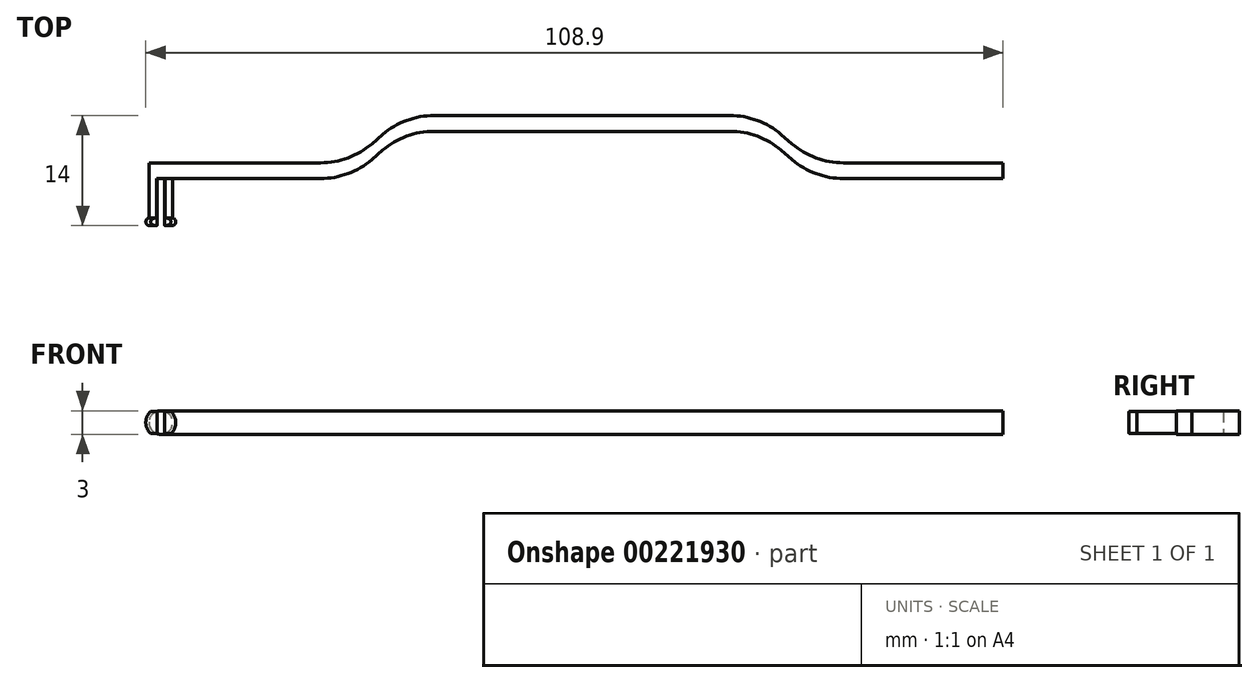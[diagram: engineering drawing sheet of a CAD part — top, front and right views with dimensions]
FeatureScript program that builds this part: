
annotation { "Feature Type Name" : "Feature", "Feature Type Description" : "" }
export const myFeature = defineFeature(function(context is Context, id is Id, definition is map)
    precondition{}
    {
        {
            var Q0;
            Q0=qCreatedBy(makeId("Top.planeOp"),FACE);
            var sketch = newSketch(context, id + "F0", { "sketchPlane" : qUnion([Q0])});
            skLineSegment(sketch, "E0.bottom", {"start": v(-53.5, 0) * mm, "end": v(-29.5, 0) * mm});
            skLineSegment(sketch, "E0.top", {"start": v(-53.5, 2) * mm, "end": v(-29.5, 2) * mm});
            skLineSegment(sketch, "E0.left", {"start": v(-53.5, 0) * mm, "end": v(-53.5, 2) * mm});
            skLineSegment(sketch, "E0.right", {"start": v(-29.5, 0) * mm, "end": v(-29.5, 2) * mm});
            skLineSegment(sketch, "E1.MirrorCS", {"start": v(29.5, 0) * mm, "end": v(29.5, 2) * mm});
            skLineSegment(sketch, "E2.MirrorCS", {"start": v(53.5, 0) * mm, "end": v(53.5, 2) * mm});
            skLineSegment(sketch, "E3.MirrorCS", {"start": v(53.5, 2) * mm, "end": v(29.5, 2) * mm});
            skLineSegment(sketch, "E4.MirrorCS", {"start": v(53.5, 0) * mm, "end": v(29.5, 0) * mm});
            skLineSegment(sketch, "E5.bottom", {"start": v(-22.5, 8) * mm, "end": v(0, 8) * mm});
            skLineSegment(sketch, "E5.top", {"start": v(-22.5, 6) * mm, "end": v(0, 6) * mm});
            skLineSegment(sketch, "E5.left", {"start": v(-22.5, 8) * mm, "end": v(-22.5, 6) * mm});
            skLineSegment(sketch, "E5.right", {"start": v(0, 8) * mm, "end": v(0, 6) * mm});
            skLineSegment(sketch, "E6.MirrorCS", {"start": v(22.5, 8) * mm, "end": v(22.5, 6) * mm});
            skLineSegment(sketch, "E7.MirrorCS", {"start": v(22.5, 8) * mm, "end": v(0, 8) * mm});
            skLineSegment(sketch, "E8.MirrorCS", {"start": v(22.5, 6) * mm, "end": v(0, 6) * mm});
            skLineSegment(sketch, "E9", {"start": v(-29.5, 0) * mm, "end": v(-22.5, 6) * mm});
            skLineSegment(sketch, "E10", {"start": v(-29.5, 2) * mm, "end": v(-22.5, 8) * mm});
            skLineSegment(sketch, "E11.MirrorCS", {"start": v(29.5, 0) * mm, "end": v(22.5, 6) * mm});
            skLineSegment(sketch, "E12.MirrorCS", {"start": v(29.5, 2) * mm, "end": v(22.5, 8) * mm});
            skLineSegment(sketch, "E13", {"start": v(-22.5, 8) * mm, "end": v(-29.5, 8) * mm, "construction": true});
            skLineSegment(sketch, "E14", {"start": v(22.5, 8) * mm, "end": v(29.5, 8) * mm, "construction": true});
            skSolve(sketch);
        }
        {
            var Q0;
            Q0 = qSketchRegion(id + "F0", true);
            extrude(context, id + "F1", {"entities" : qUnion([Q0]), "depth" : 3 * mm});
        }
        {
            var Q0;
            Q0=makeQuery(id+"F1.opExtrude","SWEPT_EDGE",EDGE,{"disambiguationData":[OSD([sQuery(id+"F0.wireOp",EDGE,"E0.top"),sQuery(id+"F0.wireOp",EDGE,"E0.right"),sQuery(id+"F0.wireOp",EDGE,"E10")])]});
            var Q1;
            Q1=makeQuery(id+"F1.opExtrude","SWEPT_EDGE",EDGE,{"disambiguationData":[OSD([sQuery(id+"F0.wireOp",EDGE,"E5.bottom"),sQuery(id+"F0.wireOp",EDGE,"E5.left"),sQuery(id+"F0.wireOp",EDGE,"E10")])]});
            var Q2;
            Q2=makeQuery(id+"F1.opExtrude","SWEPT_EDGE",EDGE,{"disambiguationData":[OSD([sQuery(id+"F0.wireOp",EDGE,"E7.MirrorCS"),sQuery(id+"F0.wireOp",EDGE,"E6.MirrorCS"),sQuery(id+"F0.wireOp",EDGE,"E12.MirrorCS")])]});
            var Q3;
            Q3=makeQuery(id+"F1.opExtrude","SWEPT_EDGE",EDGE,{"disambiguationData":[OSD([sQuery(id+"F0.wireOp",EDGE,"E3.MirrorCS"),sQuery(id+"F0.wireOp",EDGE,"E1.MirrorCS"),sQuery(id+"F0.wireOp",EDGE,"E12.MirrorCS")])]});
            var Q4;
            Q4=makeQuery(id+"F1.opExtrude","SWEPT_EDGE",EDGE,{"disambiguationData":[OSD([sQuery(id+"F0.wireOp",EDGE,"E4.MirrorCS"),sQuery(id+"F0.wireOp",EDGE,"E11.MirrorCS"),sQuery(id+"F0.wireOp",EDGE,"E1.MirrorCS")])]});
            var Q5;
            Q5=makeQuery(id+"F1.opExtrude","SWEPT_EDGE",EDGE,{"disambiguationData":[OSD([sQuery(id+"F0.wireOp",EDGE,"E8.MirrorCS"),sQuery(id+"F0.wireOp",EDGE,"E6.MirrorCS"),sQuery(id+"F0.wireOp",EDGE,"E11.MirrorCS")])]});
            var Q6;
            Q6=makeQuery(id+"F1.opExtrude","SWEPT_EDGE",EDGE,{"disambiguationData":[OSD([sQuery(id+"F0.wireOp",EDGE,"E5.top"),sQuery(id+"F0.wireOp",EDGE,"E5.left"),sQuery(id+"F0.wireOp",EDGE,"E9")])]});
            var Q7;
            Q7=makeQuery(id+"F1.opExtrude","SWEPT_EDGE",EDGE,{"disambiguationData":[OSD([sQuery(id+"F0.wireOp",EDGE,"E0.bottom"),sQuery(id+"F0.wireOp",EDGE,"E0.right"),sQuery(id+"F0.wireOp",EDGE,"E9")])]});
            fillet(context, id + "F2", {"entities" : qUnion([Q0, Q1, Q2, Q3, Q4, Q5, Q6, Q7]), "radius" : 10 * mm, "tangentPropagation" : true, "allowEdgeOverflow" : false});
        }
        {
            var Q0;
            Q0=makeQuery(id+"F1.opExtrude","SWEPT_FACE",FACE,{"disambiguationData":[OSD([sQuery(id+"F0.wireOp",EDGE,"E0.bottom")])]});
            var sketch = newSketch(context, id + "F3", { "sketchPlane" : qUnion([Q0])});
            skCircle(sketch, "E15", {"center": v(-53.5, 1.5) * mm, "radius": 1.5 * mm});
            skCircle(sketch, "E16.MirrorC", {"center": v(53.5, 1.5) * mm, "radius": 1.5 * mm});
            skSolve(sketch);
        }
        {
            var Q0;
            {var subQ1=sQuery(id+"F0.wireOp",EDGE,"E0.bottom");var subQ2=makeQuery(id+"F1.opExtrude","SWEPT_EDGE",EDGE,{"disambiguationData":[OSD([subQ1,sQuery(id+"F0.wireOp",EDGE,"E0.left")])]});Q0=makeQuery(id+"F3.imprint","IMPRINT",FACE,{"disambiguationData":[TD([[makeQuery(id+"F3.imprint","IMPRINT",EDGE,{"derivedFrom":subQ2}),-1.0]])]});}
            var Q1;
            Q1=makeQuery(id+"F3.imprint","IMPRINT",FACE,{"disambiguationData":[TD([[makeQuery(id+"F3.imprint","IMPRINT",EDGE,{"derivedFrom":sQuery(id+"F3.wireOp",EDGE,"E16.MirrorC")}),-1.0]])]});
            var Q2;
            Q2=makeQuery(id+"F1.opExtrude","SWEPT_FACE",FACE,{"disambiguationData":[OSD([sQuery(id+"F0.wireOp",EDGE,"E0.top")])]});
            extrude(context, id + "F4", {"entities" : qUnion([Q0, Q1]), "operationType" : NewBodyOperationType.ADD, "endBound" : BoundingType.UP_TO_SURFACE, "oppositeDirection" : true, "endBoundEntityFace" : qUnion([Q2]), "depth" : 25 * mm});
        }
        {
            var Q0;
            {var subQ1=sQuery(id+"F0.wireOp",EDGE,"E0.bottom");var subQ2=makeQuery(id+"F1.opExtrude","SWEPT_EDGE",EDGE,{"disambiguationData":[OSD([subQ1,sQuery(id+"F0.wireOp",EDGE,"E0.left")])]});Q0=makeQuery(id+"F3.imprint","IMPRINT",FACE,{"disambiguationData":[TD([[makeQuery(id+"F3.imprint","IMPRINT",EDGE,{"derivedFrom":subQ2}),-1.0]])]});}
            var Q1;
            {var subQ1=sQuery(id+"F0.wireOp",EDGE,"E0.bottom");var subQ2=makeQuery(id+"F1.opExtrude","SWEPT_EDGE",EDGE,{"disambiguationData":[OSD([subQ1,sQuery(id+"F0.wireOp",EDGE,"E0.left")])]});Q1=makeQuery(id+"F3.imprint","IMPRINT",FACE,{"disambiguationData":[TD([[makeQuery(id+"F3.imprint","IMPRINT",EDGE,{"derivedFrom":subQ2}),1.0]])]});}
            var Q2;
            Q2=makeQuery(id+"F3.imprint","IMPRINT",FACE,{"disambiguationData":[TD([[makeQuery(id+"F3.imprint","IMPRINT",EDGE,{"derivedFrom":sQuery(id+"F3.wireOp",EDGE,"E16.MirrorC")}),-1.0]])]});
            extrude(context, id + "F5", {"entities" : qUnion([Q0, Q1, Q2]), "operationType" : NewBodyOperationType.ADD, "depth" : 6 * mm});
        }
        {
            var Q0;
            Q0=makeQuery(id+"F5.opExtrude","CAP_FACE",FACE,{"disambiguationData":[OSD([sQuery(id+"F3.wireOp",EDGE,"E15")])],"isStart":false});
            var sketch = newSketch(context, id + "F6", { "sketchPlane" : qUnion([Q0])});
            skCircle(sketch, "E17", {"center": v(-53.5, 1.5) * mm, "radius": 1.9 * mm});
            skCircle(sketch, "E18.MirrorC", {"center": v(53.5, 1.5) * mm, "radius": 1.9 * mm});
            skSolve(sketch);
        }
        {
            var Q0;
            Q0=makeQuery(id+"F6.imprint","IMPRINT",FACE,{"disambiguationData":[TD([[makeQuery(id+"F6.imprint","IMPRINT",EDGE,{"derivedFrom":sQuery(id+"F6.wireOp",EDGE,"E17")}),1.0]])]});
            var Q1;
            Q1=makeQuery(id+"F6.imprint","IMPRINT",FACE,{"disambiguationData":[TD([[makeQuery(id+"F6.imprint","IMPRINT",EDGE,{"derivedFrom":sQuery(id+"F6.wireOp",EDGE,"E18.MirrorC")}),-1.0]])]});
            extrude(context, id + "F7", {"entities" : qUnion([Q0, Q1]), "operationType" : NewBodyOperationType.ADD, "oppositeDirection" : true, "depth" : 1 * mm});
        }
        {
            var Q0;
            Q0=makeQuery(id+"F7.opExtrude","CAP_EDGE",EDGE,{"disambiguationData":[OSD([sQuery(id+"F6.wireOp",EDGE,"E17")])],"isStart":true});
            var Q1;
            Q1=makeQuery(id+"F7.opExtrude","CAP_EDGE",EDGE,{"disambiguationData":[OSD([sQuery(id+"F6.wireOp",EDGE,"E17")])],"isStart":false});
            var Q2;
            Q2=makeQuery(id+"F7.opExtrude","CAP_EDGE",EDGE,{"disambiguationData":[OSD([sQuery(id+"F6.wireOp",EDGE,"E18.MirrorC")])],"isStart":false});
            var Q3;
            Q3=makeQuery(id+"F7.opExtrude","CAP_EDGE",EDGE,{"disambiguationData":[OSD([sQuery(id+"F6.wireOp",EDGE,"E18.MirrorC")])],"isStart":true});
            fillet(context, id + "F8", {"entities" : qUnion([Q0, Q1, Q2, Q3]), "radius" : 0.5 * mm, "tangentPropagation" : true, "allowEdgeOverflow" : false});
        }
        {
            var Q0;
            {var subQ0=sQuery(id+"F3.wireOp",EDGE,"E15");Q0=makeQuery(id+"F7.boolean.opBoolean","MERGE",FACE,{"derivedFrom":[makeQuery(id+"F5.opExtrude","CAP_FACE",FACE,{"disambiguationData":[OSD([subQ0])],"isStart":false}),makeQuery(id+"F7.opExtrude","CAP_FACE",FACE,{"disambiguationData":[OSD([subQ0,sQuery(id+"F6.wireOp",EDGE,"E17")])],"isStart":true})]});}
            var sketch = newSketch(context, id + "F9", { "sketchPlane" : qUnion([Q0])});
            skLineSegment(sketch, "E19.bottom", {"start": v(-54, -3.84) * mm, "end": v(-53, -3.84) * mm});
            skLineSegment(sketch, "E19.top", {"start": v(-54, 6.84) * mm, "end": v(-53, 6.84) * mm});
            skLineSegment(sketch, "E19.left", {"start": v(-54, -3.84) * mm, "end": v(-54, 6.84) * mm});
            skLineSegment(sketch, "E19.right", {"start": v(-53, -3.84) * mm, "end": v(-53, 6.84) * mm});
            skPoint(sketch, "E19.middle", {"position": v(-53.5, 1.5) * mm});
            skLineSegment(sketch, "E20.bottom", {"start": v(-57.96, 3.4) * mm, "end": v(-50.7, 3.4) * mm});
            skLineSegment(sketch, "E20.top", {"start": v(-57.96, 2.9) * mm, "end": v(-50.7, 2.9) * mm});
            skLineSegment(sketch, "E20.left", {"start": v(-57.96, 3.4) * mm, "end": v(-57.96, 2.9) * mm});
            skLineSegment(sketch, "E20.right", {"start": v(-50.7, 3.4) * mm, "end": v(-50.7, 2.9) * mm});
            skLineSegment(sketch, "E21.bottom", {"start": v(-57.67, -0.4) * mm, "end": v(-50.7, -0.4) * mm});
            skLineSegment(sketch, "E21.top", {"start": v(-57.67, 0.1) * mm, "end": v(-50.7, 0.1) * mm});
            skLineSegment(sketch, "E21.left", {"start": v(-57.67, -0.4) * mm, "end": v(-57.67, 0.1) * mm});
            skLineSegment(sketch, "E21.right", {"start": v(-50.7, -0.4) * mm, "end": v(-50.7, 0.1) * mm});
            skLineSegment(sketch, "E22.MirrorCS", {"start": v(57.67, -0.4) * mm, "end": v(57.67, 0.1) * mm});
            skLineSegment(sketch, "E23.MirrorCS", {"start": v(50.7, 3.4) * mm, "end": v(50.7, 2.9) * mm});
            skLineSegment(sketch, "E24.MirrorCS", {"start": v(54, -3.84) * mm, "end": v(53, -3.84) * mm});
            skLineSegment(sketch, "E25.MirrorCS", {"start": v(57.96, 3.4) * mm, "end": v(57.96, 2.9) * mm});
            skLineSegment(sketch, "E26.MirrorCS", {"start": v(50.7, -0.4) * mm, "end": v(50.7, 0.1) * mm});
            skLineSegment(sketch, "E27.MirrorCS", {"start": v(54, 6.84) * mm, "end": v(53, 6.84) * mm});
            skLineSegment(sketch, "E28.MirrorCS", {"start": v(57.96, 2.9) * mm, "end": v(50.7, 2.9) * mm});
            skPoint(sketch, "E29.MirrorP", {"position": v(53.5, 1.5) * mm});
            skLineSegment(sketch, "E30.MirrorCS", {"start": v(57.67, 0.1) * mm, "end": v(50.7, 0.1) * mm});
            skLineSegment(sketch, "E31.MirrorCS", {"start": v(57.67, -0.4) * mm, "end": v(50.7, -0.4) * mm});
            skLineSegment(sketch, "E32.MirrorCS", {"start": v(57.96, 3.4) * mm, "end": v(50.7, 3.4) * mm});
            skLineSegment(sketch, "E33.MirrorCS", {"start": v(54, -3.84) * mm, "end": v(54, 6.84) * mm});
            skLineSegment(sketch, "E34.MirrorCS", {"start": v(53, -3.84) * mm, "end": v(53, 6.84) * mm});
            skSolve(sketch);
        }
        {
            var Q0;
            Q0 = qSketchRegion(id + "F9", true);
            var Q1;
            {var subQ0=sQuery(id+"F0.wireOp",EDGE,"E0.bottom");Q1=makeQuery(id+"F4.boolean.opBoolean","MERGE",FACE,{"derivedFrom":[makeQuery(id+"F1.opExtrude","SWEPT_FACE",FACE,{"disambiguationData":[OSD([subQ0])]}),makeQuery(id+"F4.opExtrude","CAP_FACE",FACE,{"disambiguationData":[OSD([subQ0,sQuery(id+"F0.wireOp",EDGE,"E0.left"),sQuery(id+"F3.wireOp",EDGE,"E15")])],"isStart":true})]});}
            extrude(context, id + "F10", {"entities" : qUnion([Q0]), "operationType" : NewBodyOperationType.REMOVE, "endBound" : BoundingType.UP_TO_SURFACE, "oppositeDirection" : true, "endBoundEntityFace" : qUnion([Q1]), "depth" : 25 * mm});
        }
    });
